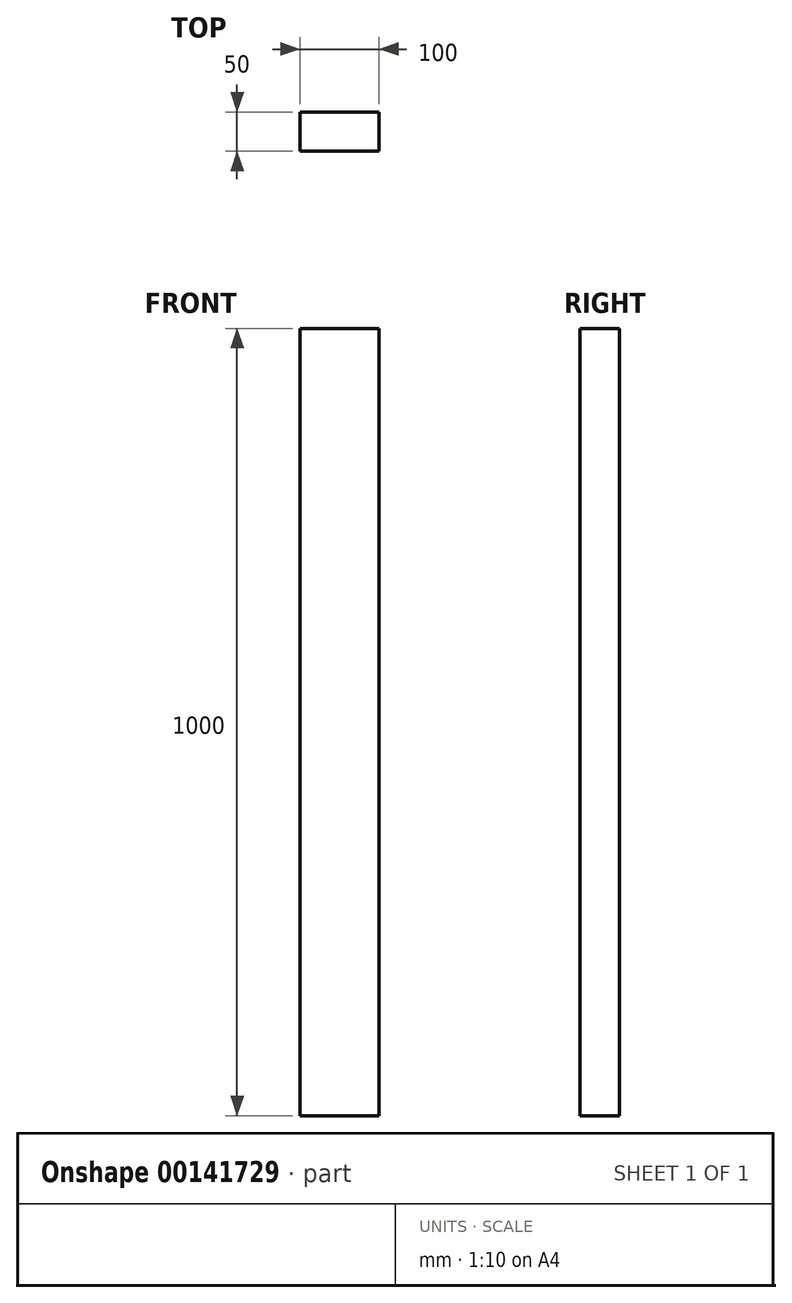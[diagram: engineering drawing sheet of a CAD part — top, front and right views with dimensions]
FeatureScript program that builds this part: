
annotation { "Feature Type Name" : "Feature", "Feature Type Description" : "" }
export const myFeature = defineFeature(function(context is Context, id is Id, definition is map)
    precondition{}
    {
        {
            var Q0;
            Q0=qCreatedBy(makeId("Top.planeOp"),FACE);
            var sketch = newSketch(context, id + "F0", { "sketchPlane" : qUnion([Q0])});
            skLineSegment(sketch, "E0.bottom", {"start": v(-50, 25) * mm, "end": v(50, 25) * mm});
            skLineSegment(sketch, "E0.top", {"start": v(-50, -25) * mm, "end": v(50, -25) * mm});
            skLineSegment(sketch, "E0.left", {"start": v(-50, 25) * mm, "end": v(-50, -25) * mm});
            skLineSegment(sketch, "E0.right", {"start": v(50, 25) * mm, "end": v(50, -25) * mm});
            skPoint(sketch, "E0.middle", {"position": v(0, 0) * mm});
            skSolve(sketch);
        }
        {
            var Q0;
            Q0 = qSketchRegion(id + "F0", true);
            extrude(context, id + "F1", {"entities" : qUnion([Q0]), "depth" : 1000 * mm});
        }
    });
